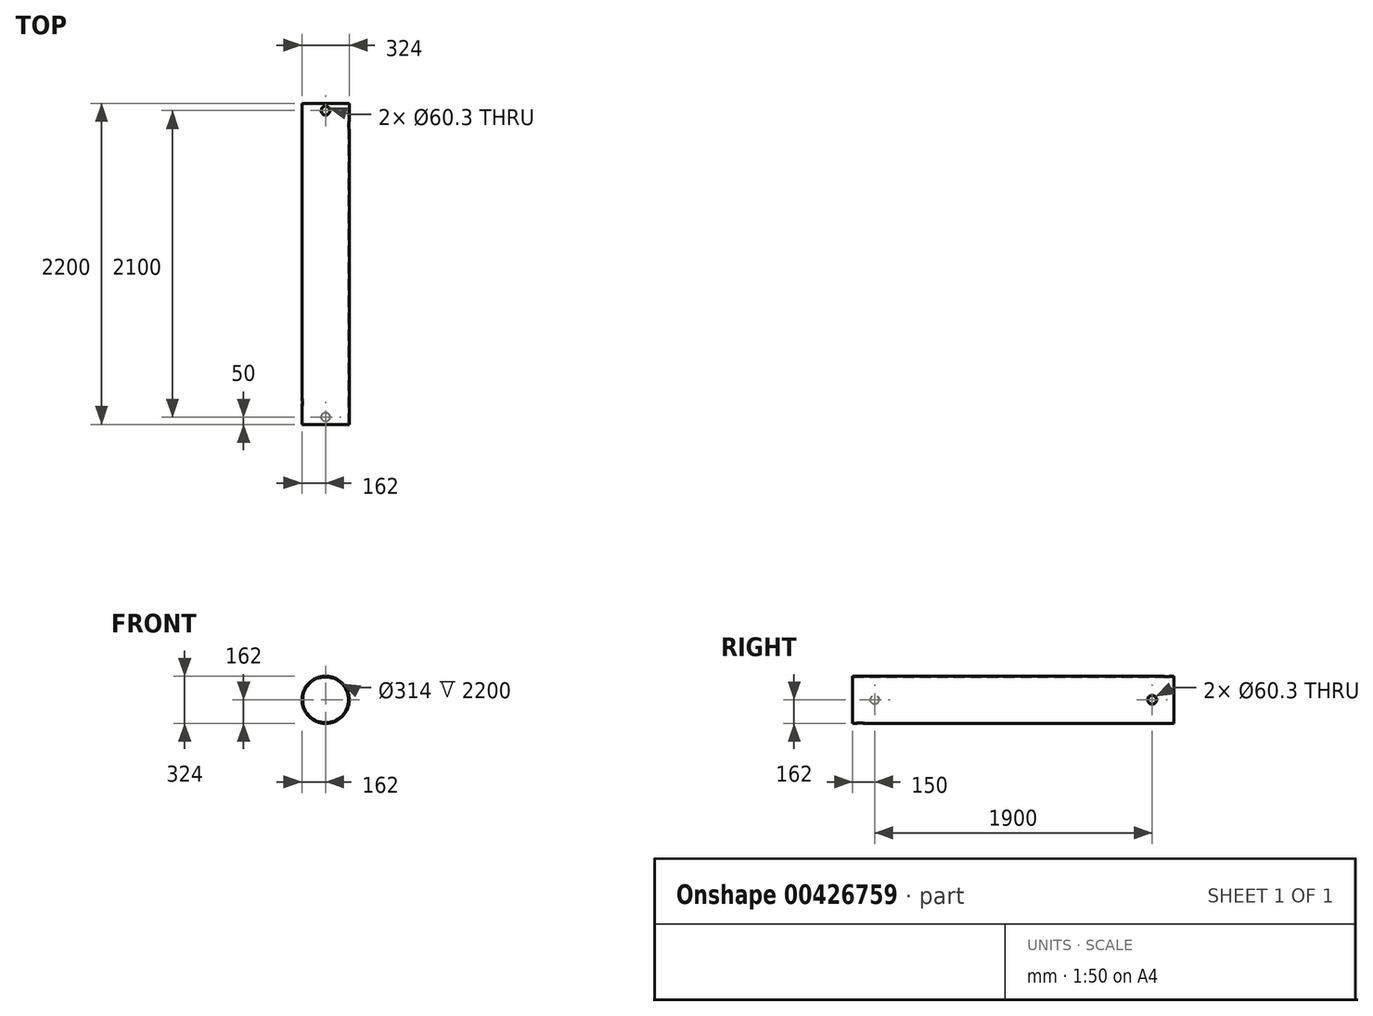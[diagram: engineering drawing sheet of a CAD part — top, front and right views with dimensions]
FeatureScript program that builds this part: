
annotation { "Feature Type Name" : "Feature", "Feature Type Description" : "" }
export const myFeature = defineFeature(function(context is Context, id is Id, definition is map)
    precondition{}
    {
        {
            var Q0;
            Q0=qCreatedBy(makeId("Front.planeOp"),FACE);
            var sketch = newSketch(context, id + "F0", { "sketchPlane" : qUnion([Q0])});
            skCircle(sketch, "E0", {"center": v(0, 0) * mm, "radius": 162 * mm});
            skCircle(sketch, "E1.0", {"center": v(0, 0) * mm, "radius": 157 * mm});
            skLineSegment(sketch, "E2", {"start": v(0, 0) * mm, "end": v(0, 162) * mm, "construction": true});
            skLineSegment(sketch, "E3", {"start": v(0, 0) * mm, "end": v(-162, 0) * mm, "construction": true});
            skSolve(sketch);
        }
        {
            var Q0;
            Q0=makeQuery(id+"F0.imprint","IMPRINT",FACE,{"disambiguationData":[TD([[makeQuery(id+"F0.imprint","IMPRINT",EDGE,{"derivedFrom":sQuery(id+"F0.wireOp",EDGE,"E0")}),1.0]])]});
            extrude(context, id + "F1", {"entities" : qUnion([Q0]), "depth" : 2200 * mm});
        }
        {
            var Q0;
            Q0=qCreatedBy(makeId("Top.planeOp"),FACE);
            var sketch = newSketch(context, id + "F2", { "sketchPlane" : qUnion([Q0])});
            skCircle(sketch, "E4", {"center": v(0, -2150) * mm, "radius": 30.15 * mm});
            skCircle(sketch, "E5", {"center": v(0, -50) * mm, "radius": 30.15 * mm});
            skSolve(sketch);
        }
        {
            var Q0;
            Q0=makeQuery(id+"F2.imprint","IMPRINT",FACE,{"disambiguationData":[TD([[makeQuery(id+"F2.imprint","IMPRINT",EDGE,{"derivedFrom":sQuery(id+"F2.wireOp",EDGE,"E5")}),1.0]])]});
            var Q1;
            Q1=makeQuery(id+"F1.opExtrude","SWEPT_FACE",FACE,{"disambiguationData":[OSD([sQuery(id+"F0.wireOp",EDGE,"E0")])]});
            extrude(context, id + "F3", {"entities" : qUnion([Q0]), "operationType" : NewBodyOperationType.REMOVE, "endBound" : BoundingType.UP_TO_SURFACE, "endBoundEntityFace" : qUnion([Q1]), "depth" : 25 * mm});
        }
        {
            var Q0;
            Q0=qCreatedBy(makeId("Right.planeOp"),FACE);
            var sketch = newSketch(context, id + "F4", { "sketchPlane" : qUnion([Q0])});
            skCircle(sketch, "E6", {"center": v(-150, 0) * mm, "radius": 30.15 * mm});
            skCircle(sketch, "E7", {"center": v(-2050, 0) * mm, "radius": 30.15 * mm});
            skSolve(sketch);
        }
        {
            var Q0;
            Q0=makeQuery(id+"F4.imprint","IMPRINT",FACE,{"disambiguationData":[TD([[makeQuery(id+"F4.imprint","IMPRINT",EDGE,{"derivedFrom":sQuery(id+"F4.wireOp",EDGE,"E6")}),1.0]])]});
            var Q1;
            Q1=makeQuery(id+"F1.opExtrude","SWEPT_FACE",FACE,{"disambiguationData":[OSD([sQuery(id+"F0.wireOp",EDGE,"E0")])]});
            extrude(context, id + "F5", {"entities" : qUnion([Q0]), "operationType" : NewBodyOperationType.REMOVE, "endBound" : BoundingType.UP_TO_SURFACE, "endBoundEntityFace" : qUnion([Q1]), "depth" : 25 * mm});
        }
        {
            var Q0;
            Q0=makeQuery(id+"F4.imprint","IMPRINT",FACE,{"disambiguationData":[TD([[makeQuery(id+"F4.imprint","IMPRINT",EDGE,{"derivedFrom":sQuery(id+"F4.wireOp",EDGE,"E7")}),1.0]])]});
            var Q1;
            Q1=makeQuery(id+"F1.opExtrude","SWEPT_FACE",FACE,{"disambiguationData":[OSD([sQuery(id+"F0.wireOp",EDGE,"E0")])]});
            extrude(context, id + "F6", {"entities" : qUnion([Q0]), "operationType" : NewBodyOperationType.REMOVE, "endBound" : BoundingType.UP_TO_SURFACE, "oppositeDirection" : true, "endBoundEntityFace" : qUnion([Q1]), "depth" : 25 * mm});
        }
        {
            var Q0;
            Q0=makeQuery(id+"F2.imprint","IMPRINT",FACE,{"disambiguationData":[TD([[makeQuery(id+"F2.imprint","IMPRINT",EDGE,{"derivedFrom":sQuery(id+"F2.wireOp",EDGE,"E4")}),1.0]])]});
            var Q1;
            Q1=makeQuery(id+"F1.opExtrude","SWEPT_FACE",FACE,{"disambiguationData":[OSD([sQuery(id+"F0.wireOp",EDGE,"E0")])]});
            extrude(context, id + "F7", {"entities" : qUnion([Q0]), "operationType" : NewBodyOperationType.REMOVE, "endBound" : BoundingType.UP_TO_SURFACE, "oppositeDirection" : true, "endBoundEntityFace" : qUnion([Q1]), "depth" : 25 * mm});
        }
    });
